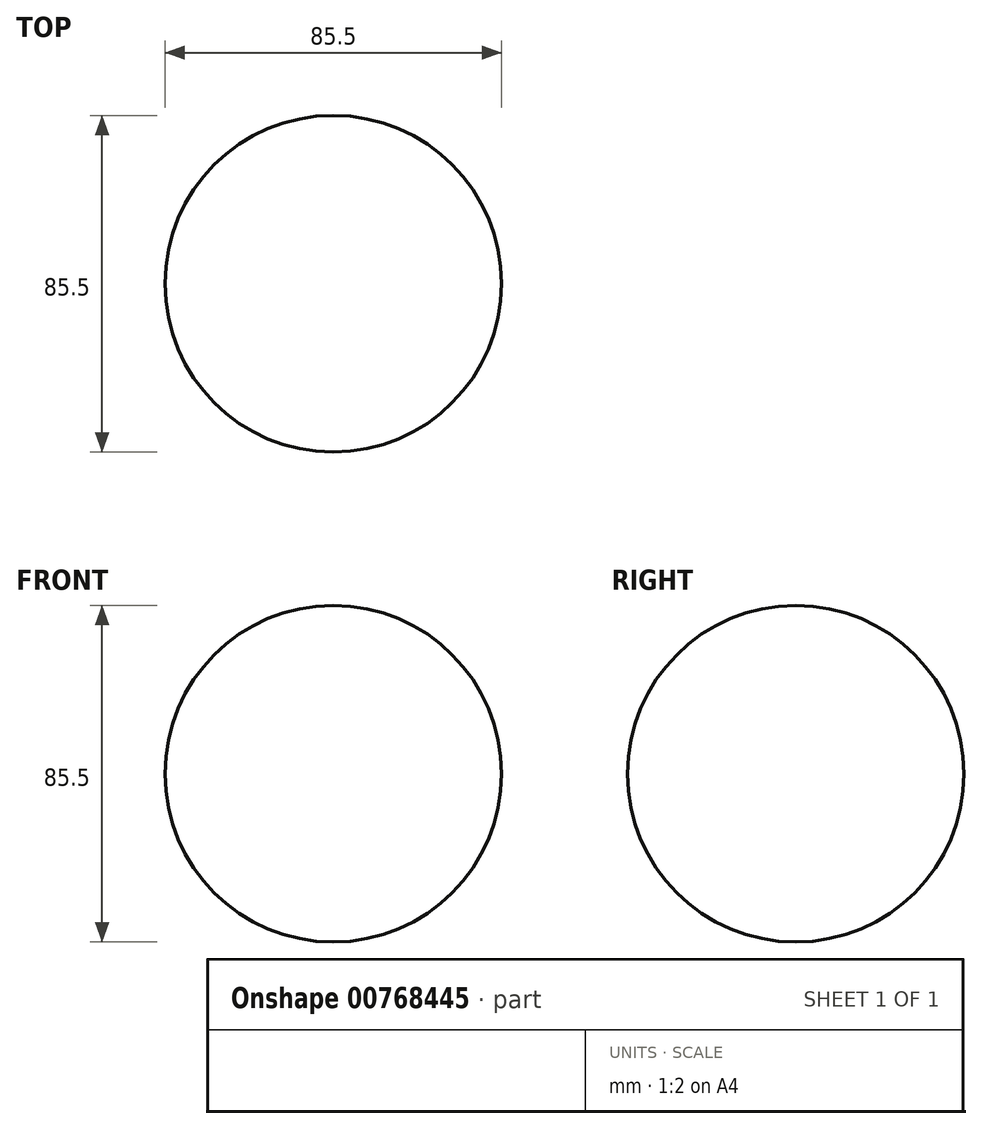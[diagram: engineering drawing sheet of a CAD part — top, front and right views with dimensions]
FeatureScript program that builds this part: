
annotation { "Feature Type Name" : "Feature", "Feature Type Description" : "" }
export const myFeature = defineFeature(function(context is Context, id is Id, definition is map)
    precondition{}
    {
        {
            var Q0;
            Q0=qCreatedBy(makeId("Front.planeOp"),FACE);
            var sketch = newSketch(context, id + "F0", { "sketchPlane" : qUnion([Q0])});
            skCircle(sketch, "E0", {"center": v(0, 0) * mm, "radius": 42.75 * mm});
            skLineSegment(sketch, "E1", {"start": v(0, 58.38) * mm, "end": v(0, -63.53) * mm});
            skSolve(sketch);
        }
        {
            var Q0;
            {var subQ0=sQuery(id+"F0.wireOp",EDGE,"E1");var subQ1=sQuery(id+"F0.wireOp",EDGE,"E0");var subQ2=makeQuery(id+"F0.imprint","INTERSECT",VERTEX,{"disambiguationData":[OD(0.0)],"derivedFrom":[subQ1,subQ0]});Q0=makeQuery(id+"F0.imprint","IMPRINT",FACE,{"disambiguationData":[TD([[makeQuery(id+"F0.imprint","IMPRINT",EDGE,{"disambiguationData":[TD([[subQ2,-1.0]])],"derivedFrom":subQ1}),1.0]])]});}
            var Q1;
            Q1=sQuery(id+"F0.wireOp",EDGE,"E1");
            revolve(context, id + "F1", {"surfaceOperationType" : NewSurfaceOperationType.NEW, "entities" : qUnion([Q0]), "axis" : qUnion([Q1]), "revolveType" : RevolveType.FULL});
        }
    });
